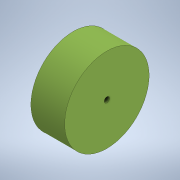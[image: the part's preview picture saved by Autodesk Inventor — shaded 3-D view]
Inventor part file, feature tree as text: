
AUTODESK INVENTOR PART (.ipt)
format: ipt  version: 2020.1 (Build 241239000, 239)  size: 95,744 bytes
history: native  units: mm
features: extrude x1, sketch x1
ambient origin geometry x8: Origin, YZ Plane, XZ Plane, XY Plane, X Axis, Y Axis, Z Axis, Center Point
bodies: Solid1 (feature_tree)
feature tree (2):
  extrude  "Extrusion1"  Depth=20.32mm
  sketch  "Sketch1"  dims[d0=50.8mm d1=3.175mm d2=20.32mm d3=0.0mm]
